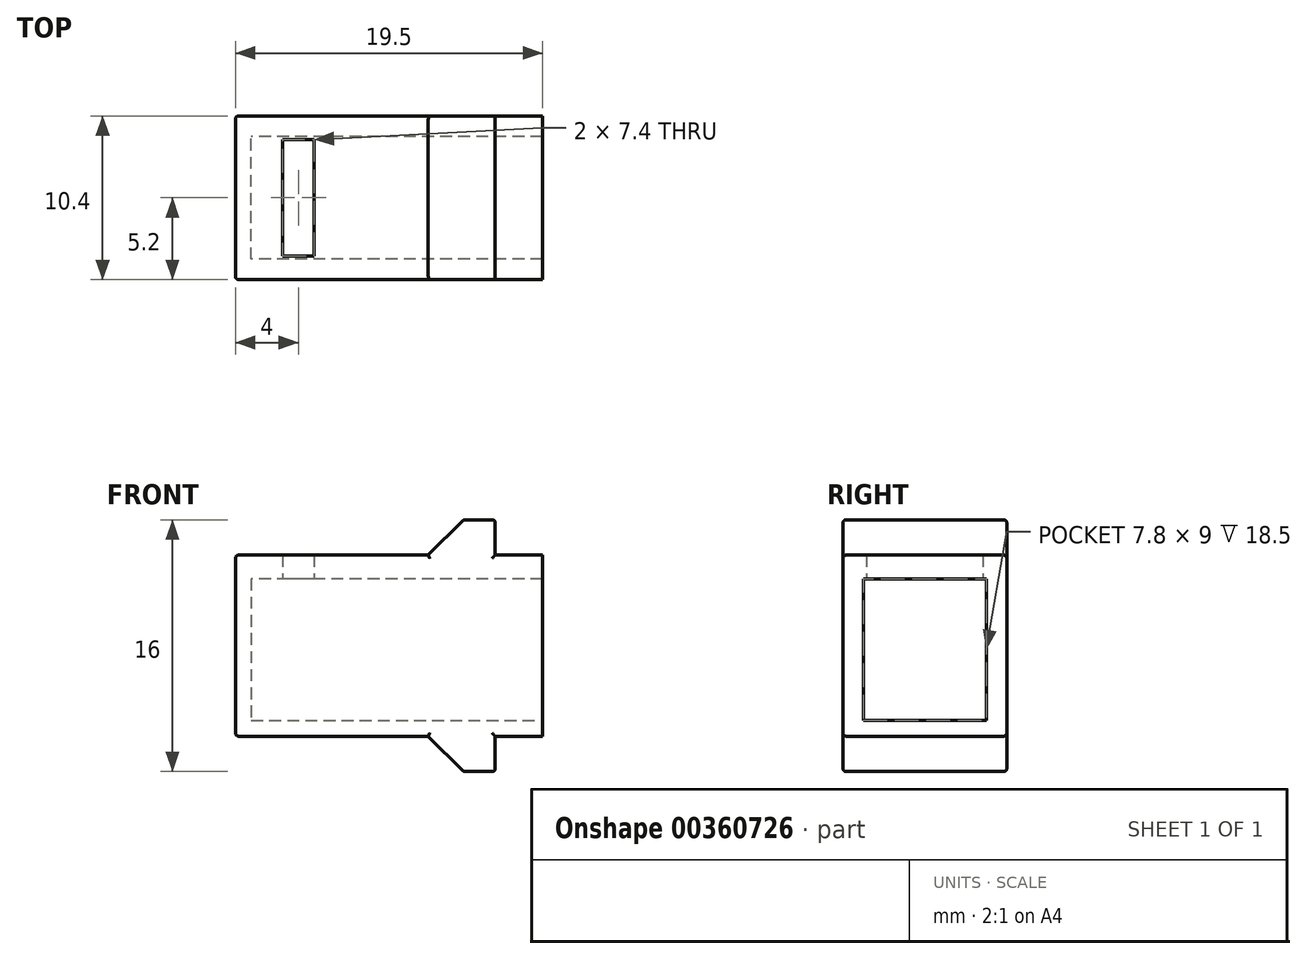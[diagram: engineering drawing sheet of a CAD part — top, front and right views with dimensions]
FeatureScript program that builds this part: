
annotation { "Feature Type Name" : "Feature", "Feature Type Description" : "" }
export const myFeature = defineFeature(function(context is Context, id is Id, definition is map)
    precondition{}
    {
        {
            var Q0;
            Q0=qCreatedBy(makeId("Front.planeOp"),FACE);
            var sketch = newSketch(context, id + "F0", { "sketchPlane" : qUnion([Q0])});
            skLineSegment(sketch, "E0.bottom", {"start": v(9.75, -5.75) * mm, "end": v(-9.75, -5.75) * mm});
            skLineSegment(sketch, "E0.top", {"start": v(9.75, 5.75) * mm, "end": v(-9.75, 5.75) * mm});
            skLineSegment(sketch, "E0.left", {"start": v(9.75, -5.75) * mm, "end": v(9.75, 5.75) * mm});
            skLineSegment(sketch, "E0.right", {"start": v(-9.75, -5.75) * mm, "end": v(-9.75, 5.75) * mm});
            skPoint(sketch, "E0.middle", {"position": v(0, 0) * mm});
            skPoint(sketch, "E1", {"position": v(-6.75, 5.75) * mm});
            skLineSegment(sketch, "E2.top", {"start": v(4.75, 8) * mm, "end": v(6.75, 8) * mm});
            skLineSegment(sketch, "E2.right", {"start": v(6.75, 5.75) * mm, "end": v(6.75, 8) * mm});
            skLineSegment(sketch, "E3", {"start": v(4.75, 8) * mm, "end": v(2.5, 5.75) * mm});
            skLineSegment(sketch, "E4.MirrorCS", {"start": v(6.75, -5.75) * mm, "end": v(6.75, -8) * mm});
            skLineSegment(sketch, "E5.MirrorCS", {"start": v(4.75, -8) * mm, "end": v(2.5, -5.75) * mm});
            skLineSegment(sketch, "E6.MirrorCS", {"start": v(4.75, -8) * mm, "end": v(6.75, -8) * mm});
            skLineSegment(sketch, "E7", {"start": v(9.75, 4.25) * mm, "end": v(-8.75, 4.25) * mm});
            skLineSegment(sketch, "E8", {"start": v(-8.75, 4.25) * mm, "end": v(-8.75, -4.75) * mm});
            skLineSegment(sketch, "E9", {"start": v(-8.75, -4.75) * mm, "end": v(9.75, -4.75) * mm});
            skLineSegment(sketch, "E10", {"start": v(-6.75, 5.75) * mm, "end": v(-6.75, 4.25) * mm});
            skLineSegment(sketch, "E11", {"start": v(-4.75, 5.75) * mm, "end": v(-4.75, 4.25) * mm});
            skSolve(sketch);
        }
        {
            var Q0;
            {var subQ6=sQuery(id+"F0.wireOp",EDGE,"E11");Q0=makeQuery(id+"F0.imprint","IMPRINT",FACE,{"disambiguationData":[TD([[makeQuery(id+"F0.imprint","IMPRINT",EDGE,{"derivedFrom":subQ6}),1.0]])]});}
            var Q1;
            Q1=makeQuery(id+"F0.imprint","IMPRINT",FACE,{"disambiguationData":[TD([[makeQuery(id+"F0.imprint","IMPRINT",EDGE,{"derivedFrom":sQuery(id+"F0.wireOp",EDGE,"E2.top")}),-1.0]])]});
            var Q2;
            {var subQ0=sQuery(id+"F0.wireOp",EDGE,"E0.right");Q2=makeQuery(id+"F0.imprint","IMPRINT",FACE,{"disambiguationData":[TD([[makeQuery(id+"F0.imprint","IMPRINT",EDGE,{"derivedFrom":subQ0}),-1.0]])]});}
            var Q3;
            {var subQ0=sQuery(id+"F0.wireOp",EDGE,"E4.MirrorCS");Q3=makeQuery(id+"F0.imprint","IMPRINT",FACE,{"disambiguationData":[TD([[makeQuery(id+"F0.imprint","IMPRINT",EDGE,{"derivedFrom":subQ0}),-1.0]])]});}
            var Q4;
            {var subQ0=sQuery(id+"F0.wireOp",EDGE,"E8");Q4=makeQuery(id+"F0.imprint","IMPRINT",FACE,{"disambiguationData":[TD([[makeQuery(id+"F0.imprint","IMPRINT",EDGE,{"derivedFrom":subQ0}),1.0]])]});}
            var Q5;
            {var subQ0=sQuery(id+"F0.wireOp",EDGE,"E10");Q5=makeQuery(id+"F0.imprint","IMPRINT",FACE,{"disambiguationData":[TD([[makeQuery(id+"F0.imprint","IMPRINT",EDGE,{"derivedFrom":subQ0}),1.0]])]});}
            extrude(context, id + "F1", {"entities" : qUnion([Q0, Q1, Q2, Q3, Q4, Q5]), "endBound" : BoundingType.SYMMETRIC, "depth" : 10.4 * mm});
        }
        {
            var Q0;
            {var subQ0=sQuery(id+"F0.wireOp",EDGE,"E10");Q0=makeQuery(id+"F0.imprint","IMPRINT",FACE,{"disambiguationData":[TD([[makeQuery(id+"F0.imprint","IMPRINT",EDGE,{"derivedFrom":subQ0}),1.0]])]});}
            extrude(context, id + "F2", {"entities" : qUnion([Q0]), "operationType" : NewBodyOperationType.REMOVE, "endBound" : BoundingType.SYMMETRIC, "depth" : 7.4 * mm});
        }
        {
            var Q0;
            {var subQ0=sQuery(id+"F0.wireOp",EDGE,"E8");Q0=makeQuery(id+"F0.imprint","IMPRINT",FACE,{"disambiguationData":[TD([[makeQuery(id+"F0.imprint","IMPRINT",EDGE,{"derivedFrom":subQ0}),1.0]])]});}
            extrude(context, id + "F3", {"entities" : qUnion([Q0]), "operationType" : NewBodyOperationType.REMOVE, "endBound" : BoundingType.SYMMETRIC, "depth" : 7.8 * mm});
        }
        {
            var Q0;
            {var subQ0=sQuery(id+"F0.wireOp",EDGE,"E0.top");var subQ1=makeQuery(id+"F0.imprint","INTERSECT",VERTEX,{"derivedFrom":[subQ0,sQuery(id+"F0.wireOp",EDGE,"E10")]});Q0=makeQuery(id+"F1.opExtrude","CAP_EDGE",EDGE,{"disambiguationData":[OSD([subQ0]),TDD([makeQuery(id+"F0.imprint","IMPRINT",EDGE,{"disambiguationData":[TD([[makeQuery(id+"F0.imprint","INTERSECT",VERTEX,{"derivedFrom":[subQ0,sQuery(id+"F0.wireOp",EDGE,"E3")]}),-1.0]])],"derivedFrom":subQ0}),makeQuery(id+"F0.imprint","IMPRINT",EDGE,{"disambiguationData":[TD([[subQ1,1.0]])],"derivedFrom":subQ0}),makeQuery(id+"F0.imprint","IMPRINT",EDGE,{"disambiguationData":[TD([[makeQuery(id+"F0.imprint","INTERSECT",VERTEX,{"derivedFrom":[subQ0,sQuery(id+"F0.wireOp",EDGE,"E0.right")]}),1.0]])],"derivedFrom":subQ0})])],"isStart":false});}
            var Q1;
            Q1=makeQuery(id+"F1.opExtrude","CAP_EDGE",EDGE,{"disambiguationData":[OSD([sQuery(id+"F0.wireOp",EDGE,"E3")])],"isStart":false});
            var Q2;
            Q2=makeQuery(id+"F1.opExtrude","SWEPT_EDGE",EDGE,{"disambiguationData":[OSD([sQuery(id+"F0.wireOp",EDGE,"E2.top"),sQuery(id+"F0.wireOp",EDGE,"E2.right")])]});
            var Q3;
            Q3=makeQuery(id+"F1.opExtrude","SWEPT_EDGE",EDGE,{"disambiguationData":[OSD([sQuery(id+"F0.wireOp",EDGE,"E2.top"),sQuery(id+"F0.wireOp",EDGE,"E3")])]});
            var Q4;
            Q4=makeQuery(id+"F1.opExtrude","CAP_EDGE",EDGE,{"disambiguationData":[OSD([sQuery(id+"F0.wireOp",EDGE,"E2.top")])],"isStart":false});
            var Q5;
            Q5=makeQuery(id+"F1.opExtrude","CAP_EDGE",EDGE,{"disambiguationData":[OSD([sQuery(id+"F0.wireOp",EDGE,"E2.right")])],"isStart":false});
            var Q6;
            {var subQ0=sQuery(id+"F0.wireOp",EDGE,"E0.top");Q6=makeQuery(id+"F1.opExtrude","CAP_EDGE",EDGE,{"disambiguationData":[OSD([subQ0]),TDD([makeQuery(id+"F0.imprint","IMPRINT",EDGE,{"disambiguationData":[TD([[makeQuery(id+"F0.imprint","INTERSECT",VERTEX,{"derivedFrom":[subQ0,sQuery(id+"F0.wireOp",EDGE,"E0.left")]}),-1.0]])],"derivedFrom":subQ0})])],"isStart":false});}
            var Q7;
            {var subQ0=sQuery(id+"F0.wireOp",EDGE,"E0.top");Q7=makeQuery(id+"F1.opExtrude","CAP_EDGE",EDGE,{"disambiguationData":[OSD([subQ0]),TDD([makeQuery(id+"F0.imprint","IMPRINT",EDGE,{"disambiguationData":[TD([[makeQuery(id+"F0.imprint","INTERSECT",VERTEX,{"derivedFrom":[subQ0,sQuery(id+"F0.wireOp",EDGE,"E0.left")]}),-1.0]])],"derivedFrom":subQ0})])],"isStart":true});}
            var Q8;
            {var subQ0=sQuery(id+"F0.wireOp",EDGE,"E0.top");var subQ1=makeQuery(id+"F0.imprint","INTERSECT",VERTEX,{"derivedFrom":[subQ0,sQuery(id+"F0.wireOp",EDGE,"E10")]});Q8=makeQuery(id+"F1.opExtrude","CAP_EDGE",EDGE,{"disambiguationData":[OSD([subQ0]),TDD([makeQuery(id+"F0.imprint","IMPRINT",EDGE,{"disambiguationData":[TD([[makeQuery(id+"F0.imprint","INTERSECT",VERTEX,{"derivedFrom":[subQ0,sQuery(id+"F0.wireOp",EDGE,"E3")]}),-1.0]])],"derivedFrom":subQ0}),makeQuery(id+"F0.imprint","IMPRINT",EDGE,{"disambiguationData":[TD([[subQ1,1.0]])],"derivedFrom":subQ0}),makeQuery(id+"F0.imprint","IMPRINT",EDGE,{"disambiguationData":[TD([[makeQuery(id+"F0.imprint","INTERSECT",VERTEX,{"derivedFrom":[subQ0,sQuery(id+"F0.wireOp",EDGE,"E0.right")]}),1.0]])],"derivedFrom":subQ0})])],"isStart":true});}
            var Q9;
            Q9=makeQuery(id+"F1.opExtrude","CAP_EDGE",EDGE,{"disambiguationData":[OSD([sQuery(id+"F0.wireOp",EDGE,"E3")])],"isStart":true});
            var Q10;
            Q10=makeQuery(id+"F1.opExtrude","CAP_EDGE",EDGE,{"disambiguationData":[OSD([sQuery(id+"F0.wireOp",EDGE,"E2.top")])],"isStart":true});
            var Q11;
            Q11=makeQuery(id+"F1.opExtrude","SWEPT_EDGE",EDGE,{"disambiguationData":[OSD([sQuery(id+"F0.wireOp",EDGE,"E0.top"),sQuery(id+"F0.wireOp",EDGE,"E0.right")])]});
            var Q12;
            Q12=makeQuery(id+"F1.opExtrude","CAP_EDGE",EDGE,{"disambiguationData":[OSD([sQuery(id+"F0.wireOp",EDGE,"E0.right")])],"isStart":false});
            var Q13;
            {var subQ0=sQuery(id+"F0.wireOp",EDGE,"E0.bottom");Q13=makeQuery(id+"F1.opExtrude","CAP_EDGE",EDGE,{"disambiguationData":[OSD([subQ0]),TDD([makeQuery(id+"F0.imprint","IMPRINT",EDGE,{"disambiguationData":[TD([[makeQuery(id+"F0.imprint","INTERSECT",VERTEX,{"derivedFrom":[subQ0,sQuery(id+"F0.wireOp",EDGE,"E0.right")]}),1.0]])],"derivedFrom":subQ0})])],"isStart":false});}
            var Q14;
            Q14=makeQuery(id+"F1.opExtrude","CAP_EDGE",EDGE,{"disambiguationData":[OSD([sQuery(id+"F0.wireOp",EDGE,"E6.MirrorCS")])],"isStart":false});
            var Q15;
            {var subQ0=sQuery(id+"F0.wireOp",EDGE,"E0.bottom");Q15=makeQuery(id+"F1.opExtrude","CAP_EDGE",EDGE,{"disambiguationData":[OSD([subQ0]),TDD([makeQuery(id+"F0.imprint","IMPRINT",EDGE,{"disambiguationData":[TD([[makeQuery(id+"F0.imprint","INTERSECT",VERTEX,{"derivedFrom":[subQ0,sQuery(id+"F0.wireOp",EDGE,"E0.left")]}),-1.0]])],"derivedFrom":subQ0})])],"isStart":false});}
            var Q16;
            Q16=makeQuery(id+"F1.opExtrude","SWEPT_EDGE",EDGE,{"disambiguationData":[OSD([sQuery(id+"F0.wireOp",EDGE,"E4.MirrorCS"),sQuery(id+"F0.wireOp",EDGE,"E6.MirrorCS")])]});
            var Q17;
            Q17=makeQuery(id+"F1.opExtrude","SWEPT_EDGE",EDGE,{"disambiguationData":[OSD([sQuery(id+"F0.wireOp",EDGE,"E5.MirrorCS"),sQuery(id+"F0.wireOp",EDGE,"E6.MirrorCS")])]});
            var Q18;
            Q18=makeQuery(id+"F1.opExtrude","CAP_EDGE",EDGE,{"disambiguationData":[OSD([sQuery(id+"F0.wireOp",EDGE,"E5.MirrorCS")])],"isStart":true});
            var Q19;
            Q19=makeQuery(id+"F1.opExtrude","CAP_EDGE",EDGE,{"disambiguationData":[OSD([sQuery(id+"F0.wireOp",EDGE,"E5.MirrorCS")])],"isStart":false});
            var Q20;
            Q20=makeQuery(id+"F1.opExtrude","CAP_EDGE",EDGE,{"disambiguationData":[OSD([sQuery(id+"F0.wireOp",EDGE,"E6.MirrorCS")])],"isStart":true});
            var Q21;
            {var subQ0=sQuery(id+"F0.wireOp",EDGE,"E0.bottom");Q21=makeQuery(id+"F1.opExtrude","CAP_EDGE",EDGE,{"disambiguationData":[OSD([subQ0]),TDD([makeQuery(id+"F0.imprint","IMPRINT",EDGE,{"disambiguationData":[TD([[makeQuery(id+"F0.imprint","INTERSECT",VERTEX,{"derivedFrom":[subQ0,sQuery(id+"F0.wireOp",EDGE,"E0.right")]}),1.0]])],"derivedFrom":subQ0})])],"isStart":true});}
            var Q22;
            {var subQ0=sQuery(id+"F0.wireOp",EDGE,"E0.bottom");Q22=makeQuery(id+"F1.opExtrude","CAP_EDGE",EDGE,{"disambiguationData":[OSD([subQ0]),TDD([makeQuery(id+"F0.imprint","IMPRINT",EDGE,{"disambiguationData":[TD([[makeQuery(id+"F0.imprint","INTERSECT",VERTEX,{"derivedFrom":[subQ0,sQuery(id+"F0.wireOp",EDGE,"E0.left")]}),-1.0]])],"derivedFrom":subQ0})])],"isStart":true});}
            var Q23;
            Q23=makeQuery(id+"F1.opExtrude","CAP_EDGE",EDGE,{"disambiguationData":[OSD([sQuery(id+"F0.wireOp",EDGE,"E4.MirrorCS")])],"isStart":true});
            var Q24;
            Q24=makeQuery(id+"F1.opExtrude","SWEPT_FACE",FACE,{"disambiguationData":[OSD([sQuery(id+"F0.wireOp",EDGE,"E0.right")])]});
            var Q25;
            Q25=makeQuery(id+"F1.opExtrude","CAP_EDGE",EDGE,{"disambiguationData":[OSD([sQuery(id+"F0.wireOp",EDGE,"E2.right")])],"isStart":true});
            var Q26;
            Q26=makeQuery(id+"F1.opExtrude","CAP_EDGE",EDGE,{"disambiguationData":[OSD([sQuery(id+"F0.wireOp",EDGE,"E4.MirrorCS")])],"isStart":false});
            fillet(context, id + "F4", {"entities" : qUnion([Q0, Q1, Q2, Q3, Q4, Q5, Q6, Q7, Q8, Q9, Q10, Q11, Q12, Q13, Q14, Q15, Q16, Q17, Q18, Q19, Q20, Q21, Q22, Q23, Q24, Q25, Q26]), "radius" : .2 * mm, "tangentPropagation" : true, "allowEdgeOverflow" : false});
        }
    });
